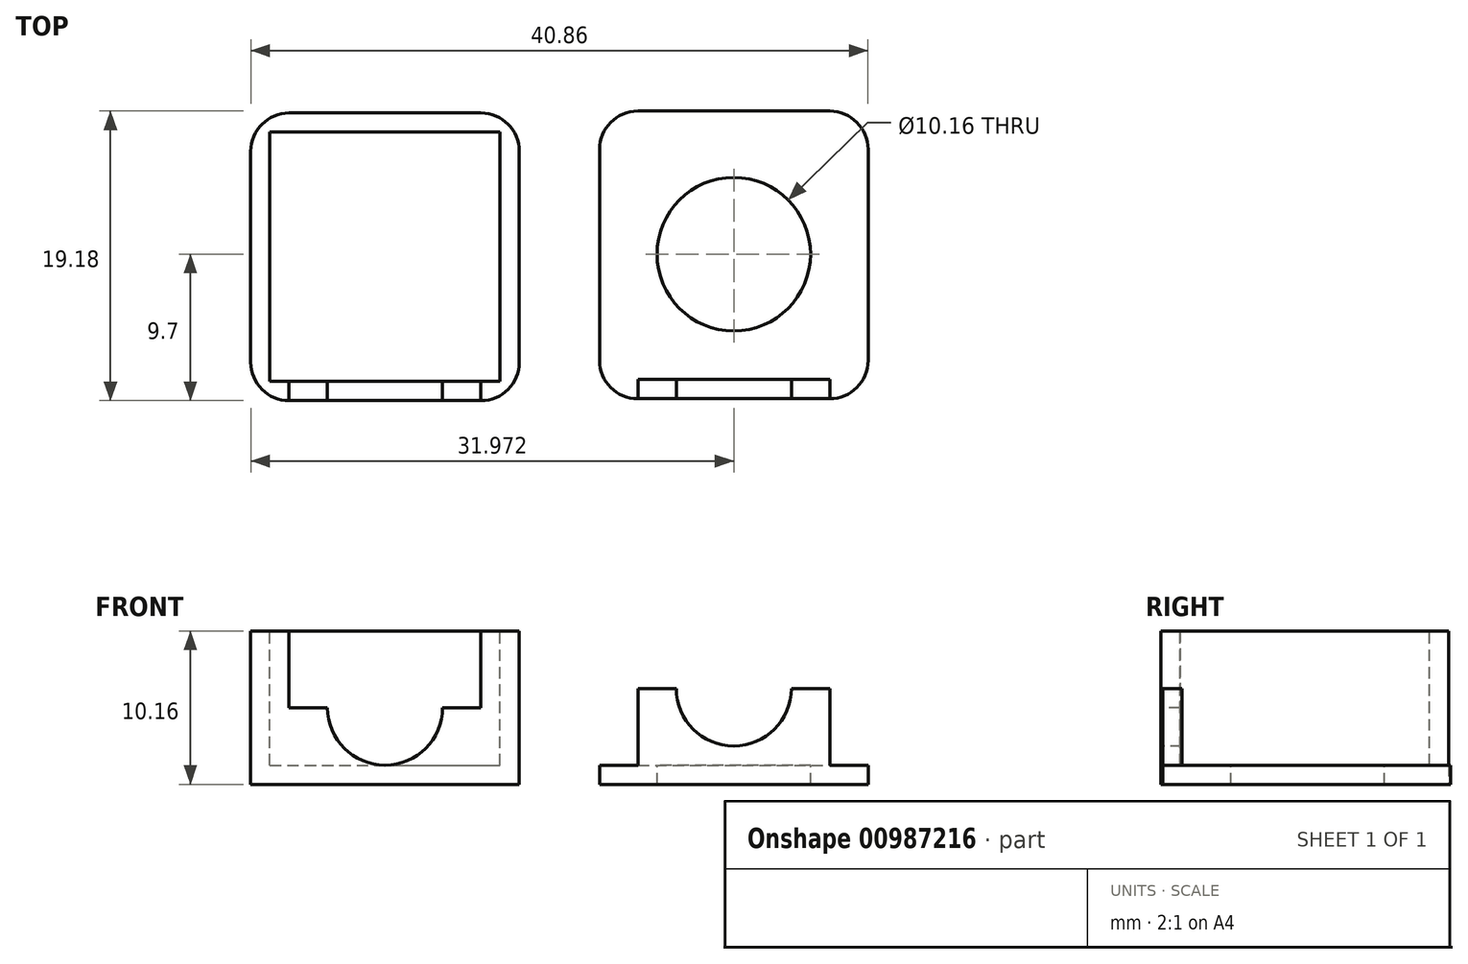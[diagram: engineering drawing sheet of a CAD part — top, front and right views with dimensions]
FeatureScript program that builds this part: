
annotation { "Feature Type Name" : "Feature", "Feature Type Description" : "" }
export const myFeature = defineFeature(function(context is Context, id is Id, definition is map)
    precondition{}
    {
        {
            var Q0;
            Q0=qCreatedBy(makeId("Top.planeOp"),FACE);
            var sketch = newSketch(context, id + "F0", { "sketchPlane" : qUnion([Q0])});
            skLineSegment(sketch, "E0.bottom", {"start": v(-7.63, 9.35) * mm, "end": v(10.15, 9.35) * mm});
            skLineSegment(sketch, "E0.top", {"start": v(-7.63, -9.7) * mm, "end": v(10.15, -9.7) * mm});
            skLineSegment(sketch, "E0.left", {"start": v(-7.63, 9.35) * mm, "end": v(-7.63, -9.7) * mm});
            skLineSegment(sketch, "E0.right", {"start": v(10.15, 9.35) * mm, "end": v(10.15, -9.7) * mm});
            skSolve(sketch);
        }
        {
            var Q0;
            Q0 = qSketchRegion(id + "F0", true);
            extrude(context, id + "F1", {"entities" : qUnion([Q0]), "depth" : 10.16 * mm, "offsetDistance" : 25.4 * mm});
        }
        {
            var Q0;
            Q0=makeQuery(id+"F1.opExtrude","CAP_FACE",FACE,{"disambiguationData":[OSD([sQuery(id+"F0.wireOp",EDGE,"E0.bottom"),sQuery(id+"F0.wireOp",EDGE,"E0.top"),sQuery(id+"F0.wireOp",EDGE,"E0.left"),sQuery(id+"F0.wireOp",EDGE,"E0.right")])],"isStart":false});
            var sketch = newSketch(context, id + "F2", { "sketchPlane" : qUnion([Q0])});
            skLineSegment(sketch, "E1", {"start": v(-6.36, 8.08) * mm, "end": v(8.88, 8.08) * mm});
            skLineSegment(sketch, "E2", {"start": v(-6.36, 8.08) * mm, "end": v(-6.36, -8.43) * mm});
            skLineSegment(sketch, "E3", {"start": v(-6.36, -8.43) * mm, "end": v(8.88, -8.43) * mm});
            skLineSegment(sketch, "E4", {"start": v(8.88, 8.08) * mm, "end": v(8.88, -8.43) * mm});
            skSolve(sketch);
        }
        {
            var Q0;
            Q0=makeQuery(id+"F2.imprint","IMPRINT",FACE,{"disambiguationData":[TD([[makeQuery(id+"F2.imprint","IMPRINT",EDGE,{"derivedFrom":sQuery(id+"F2.wireOp",EDGE,"E1")}),-1.0]])]});
            extrude(context, id + "F3", {"entities" : qUnion([Q0]), "operationType" : NewBodyOperationType.REMOVE, "oppositeDirection" : true, "depth" : 8.9 * mm, "offsetDistance" : 25.4 * mm});
        }
        {
            var Q0;
            Q0=makeQuery(id+"F1.opExtrude","SWEPT_EDGE",EDGE,{"disambiguationData":[OSD([sQuery(id+"F0.wireOp",EDGE,"E0.bottom"),sQuery(id+"F0.wireOp",EDGE,"E0.right")])]});
            var Q1;
            Q1=makeQuery(id+"F1.opExtrude","SWEPT_EDGE",EDGE,{"disambiguationData":[OSD([sQuery(id+"F0.wireOp",EDGE,"E0.bottom"),sQuery(id+"F0.wireOp",EDGE,"E0.left")])]});
            var Q2;
            Q2=makeQuery(id+"F1.opExtrude","SWEPT_EDGE",EDGE,{"disambiguationData":[OSD([sQuery(id+"F0.wireOp",EDGE,"E0.top"),sQuery(id+"F0.wireOp",EDGE,"E0.left")])]});
            var Q3;
            Q3=makeQuery(id+"F1.opExtrude","SWEPT_EDGE",EDGE,{"disambiguationData":[OSD([sQuery(id+"F0.wireOp",EDGE,"E0.top"),sQuery(id+"F0.wireOp",EDGE,"E0.right")])]});
            fillet(context, id + "F4", {"entities" : qUnion([Q0, Q1, Q2, Q3]), "radius" : 2.54 * mm, "tangentPropagation" : true, "allowEdgeOverflow" : false});
        }
        {
            var Q0;
            Q0=makeQuery(id+"F1.opExtrude","SWEPT_FACE",FACE,{"disambiguationData":[OSD([sQuery(id+"F0.wireOp",EDGE,"E0.top")])]});
            var sketch = newSketch(context, id + "F5", { "sketchPlane" : qUnion([Q0])});
            skCircle(sketch, "E5", {"center": v(1.26, 5.08) * mm, "radius": 3.81 * mm});
            skPoint(sketch, "E5.centerSnap0", {"position": v(-5.1, 5.08) * mm});
            skPoint(sketch, "E5.centerSnap1", {"position": v(1.26, 10.16) * mm});
            skLineSegment(sketch, "E6", {"start": v(-5.1, 5.08) * mm, "end": v(-2.55, 5.08) * mm});
            skLineSegment(sketch, "E7", {"start": v(-2.55, 5.08) * mm, "end": v(-2.55, 10.16) * mm});
            skLineSegment(sketch, "E8", {"start": v(-2.55, 10.16) * mm, "end": v(-5.1, 10.16) * mm});
            skLineSegment(sketch, "E9", {"start": v(-5.1, 10.16) * mm, "end": v(-5.1, 5.08) * mm});
            skLineSegment(sketch, "E10", {"start": v(7.6, 5.08) * mm, "end": v(5.07, 5.08) * mm});
            skLineSegment(sketch, "E11", {"start": v(5.07, 5.08) * mm, "end": v(5.07, 10.16) * mm});
            skLineSegment(sketch, "E12", {"start": v(5.07, 10.16) * mm, "end": v(7.6, 10.16) * mm});
            skLineSegment(sketch, "E13", {"start": v(7.6, 10.16) * mm, "end": v(7.6, 5.08) * mm});
            skSolve(sketch);
        }
        {
            var Q0;
            Q0 = qSketchRegion(id + "F5", true);
            var Q1;
            {var subQ0=sQuery(id+"F5.wireOp",EDGE,"kxRTGXXc-5I6O-ZEoy-Imr0-OJisQxjdW8h1");Q1=makeQuery(id+"F5.imprint","IMPRINT",FACE,{"disambiguationData":[TD([[makeQuery(id+"F5.imprint","IMPRINT",EDGE,{"derivedFrom":subQ0}),-1.0]])]});}
            var Q2;
            {var subQ0=sQuery(id+"F5.wireOp",EDGE,"E7");Q2=makeQuery(id+"F5.imprint","IMPRINT",FACE,{"disambiguationData":[TD([[makeQuery(id+"F5.imprint","IMPRINT",EDGE,{"derivedFrom":subQ0}),-1.0]])]});}
            extrude(context, id + "F6", {"entities" : qUnion([Q0, Q1, Q2]), "operationType" : NewBodyOperationType.REMOVE, "oppositeDirection" : true, "depth" : 1.27 * mm, "offsetDistance" : 25.4 * mm});
        }
        {
            var Q0;
            Q0=qCreatedBy(makeId("Top.planeOp"),FACE);
            var sketch = newSketch(context, id + "F7", { "sketchPlane" : qUnion([Q0])});
            skLineSegment(sketch, "E14.bottom", {"start": v(15.45, 9.48) * mm, "end": v(33.23, 9.48) * mm});
            skLineSegment(sketch, "E14.top", {"start": v(15.45, -9.57) * mm, "end": v(33.23, -9.57) * mm});
            skLineSegment(sketch, "E14.left", {"start": v(15.45, 9.48) * mm, "end": v(15.45, -9.57) * mm});
            skLineSegment(sketch, "E14.right", {"start": v(33.23, 9.48) * mm, "end": v(33.23, -9.57) * mm});
            skSolve(sketch);
        }
        {
            var Q0;
            Q0 = qSketchRegion(id + "F7", true);
            extrude(context, id + "F8", {"entities" : qUnion([Q0]), "depth" : 1.27 * mm, "offsetDistance" : 25.4 * mm});
        }
        {
            var Q0;
            Q0=makeQuery(id+"F8.opExtrude","SWEPT_EDGE",EDGE,{"disambiguationData":[OSD([sQuery(id+"F7.wireOp",EDGE,"E14.top"),sQuery(id+"F7.wireOp",EDGE,"E14.left")])]});
            var Q1;
            Q1=makeQuery(id+"F8.opExtrude","SWEPT_EDGE",EDGE,{"disambiguationData":[OSD([sQuery(id+"F7.wireOp",EDGE,"E14.top"),sQuery(id+"F7.wireOp",EDGE,"E14.right")])]});
            var Q2;
            Q2=makeQuery(id+"F8.opExtrude","SWEPT_EDGE",EDGE,{"disambiguationData":[OSD([sQuery(id+"F7.wireOp",EDGE,"E14.bottom"),sQuery(id+"F7.wireOp",EDGE,"E14.right")])]});
            var Q3;
            Q3=makeQuery(id+"F8.opExtrude","SWEPT_EDGE",EDGE,{"disambiguationData":[OSD([sQuery(id+"F7.wireOp",EDGE,"E14.bottom"),sQuery(id+"F7.wireOp",EDGE,"E14.left")])]});
            fillet(context, id + "F9", {"entities" : qUnion([Q0, Q1, Q2, Q3]), "radius" : 2.54 * mm, "tangentPropagation" : true, "allowEdgeOverflow" : false});
        }
        {
            var Q0;
            Q0=makeQuery(id+"F8.opExtrude","CAP_FACE",FACE,{"disambiguationData":[OSD([sQuery(id+"F7.wireOp",EDGE,"E14.bottom"),sQuery(id+"F7.wireOp",EDGE,"E14.top"),sQuery(id+"F7.wireOp",EDGE,"E14.left"),sQuery(id+"F7.wireOp",EDGE,"E14.right")])],"isStart":false});
            var sketch = newSketch(context, id + "F10", { "sketchPlane" : qUnion([Q0])});
            skLineSegment(sketch, "E15", {"start": v(18, -9.57) * mm, "end": v(18, -8.3) * mm});
            skLineSegment(sketch, "E16", {"start": v(30.7, -9.57) * mm, "end": v(30.7, -8.3) * mm});
            skLineSegment(sketch, "E17", {"start": v(18, -8.3) * mm, "end": v(30.7, -8.3) * mm});
            skLineSegment(sketch, "E18", {"start": v(18, -9.57) * mm, "end": v(30.7, -9.57) * mm});
            skSolve(sketch);
        }
        {
            var Q0;
            Q0=makeQuery(id+"F10.imprint","IMPRINT",FACE,{"disambiguationData":[TD([[makeQuery(id+"F10.imprint","IMPRINT",EDGE,{"derivedFrom":sQuery(id+"F10.wireOp",EDGE,"E15")}),-1.0]])]});
            extrude(context, id + "F11", {"entities" : qUnion([Q0]), "operationType" : NewBodyOperationType.ADD, "depth" : 5.08 * mm, "offsetDistance" : 25.4 * mm});
        }
        {
            var Q0;
            Q0=makeQuery(id+"F11.boolean.opBoolean","MERGE",FACE,{"derivedFrom":[makeQuery(id+"F8.opExtrude","SWEPT_FACE",FACE,{"disambiguationData":[OSD([sQuery(id+"F7.wireOp",EDGE,"E14.top")])]}),makeQuery(id+"F11.opExtrude","SWEPT_FACE",FACE,{"disambiguationData":[OSD([sQuery(id+"F10.wireOp",EDGE,"E18")])]})]});
            var sketch = newSketch(context, id + "F12", { "sketchPlane" : qUnion([Q0])});
            skCircle(sketch, "E19", {"center": v(24.34, 6.35) * mm, "radius": 3.81 * mm});
            skSolve(sketch);
        }
        {
            var Q0;
            Q0 = qSketchRegion(id + "F12", true);
            extrude(context, id + "F13", {"entities" : qUnion([Q0]), "operationType" : NewBodyOperationType.REMOVE, "oppositeDirection" : true, "depth" : 1.27 * mm, "offsetDistance" : 25.4 * mm});
        }
        {
            var Q0;
            Q0=makeQuery(id+"F8.opExtrude","CAP_FACE",FACE,{"disambiguationData":[OSD([sQuery(id+"F7.wireOp",EDGE,"E14.bottom"),sQuery(id+"F7.wireOp",EDGE,"E14.top"),sQuery(id+"F7.wireOp",EDGE,"E14.left"),sQuery(id+"F7.wireOp",EDGE,"E14.right")])],"isStart":false});
            var sketch = newSketch(context, id + "F14", { "sketchPlane" : qUnion([Q0])});
            skCircle(sketch, "E20", {"center": v(24.34, 0) * mm, "radius": 5.08 * mm});
            skPoint(sketch, "E20.centerSnap0", {"position": v(24.34, 9.48) * mm});
            skSolve(sketch);
        }
        {
            var Q0;
            Q0 = qSketchRegion(id + "F14", true);
            extrude(context, id + "F15", {"entities" : qUnion([Q0]), "operationType" : NewBodyOperationType.REMOVE, "oppositeDirection" : true, "depth" : 1.27 * mm, "offsetDistance" : 25.4 * mm});
        }
    });
